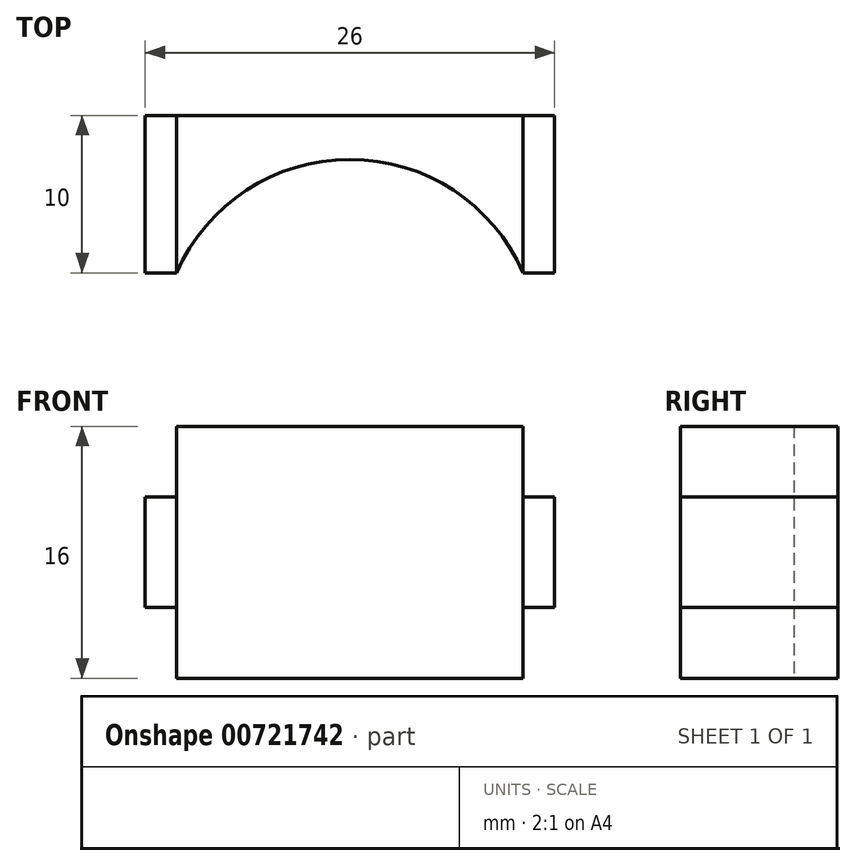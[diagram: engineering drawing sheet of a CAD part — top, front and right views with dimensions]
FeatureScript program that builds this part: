
annotation { "Feature Type Name" : "Feature", "Feature Type Description" : "" }
export const myFeature = defineFeature(function(context is Context, id is Id, definition is map)
    precondition{}
    {
        {
            var Q0;
            Q0=qCreatedBy(makeId("Top.planeOp"),FACE);
            var sketch = newSketch(context, id + "F0", { "sketchPlane" : qUnion([Q0])});
            skLineSegment(sketch, "E0", {"start": v(0, 0) * mm, "end": v(0, 10) * mm});
            skLineSegment(sketch, "E1", {"start": v(0, 10) * mm, "end": v(22, 10) * mm});
            skLineSegment(sketch, "E2", {"start": v(22, 10) * mm, "end": v(22, 0) * mm});
            skArc(sketch, "E3", {"start": v(22, 0) * mm, "mid": v(11, 7.2) * mm, "end": v(0, 0) * mm});
            skSolve(sketch);
        }
        {
            var Q0;
            Q0 = qSketchRegion(id + "F0", true);
            extrude(context, id + "F1", {"entities" : qUnion([Q0]), "depth" : 16 * mm, "offsetDistance" : 25 * mm});
        }
        {
            var Q0;
            Q0=makeQuery(id+"F1.opExtrude","SWEPT_FACE",FACE,{"disambiguationData":[OSD([sQuery(id+"F0.wireOp",EDGE,"E2")])]});
            var sketch = newSketch(context, id + "F2", { "sketchPlane" : qUnion([Q0])});
            skLineSegment(sketch, "E4.bottom", {"start": v(10, 11.5) * mm, "end": v(0, 11.5) * mm});
            skLineSegment(sketch, "E4.top", {"start": v(10, 4.5) * mm, "end": v(0, 4.5) * mm});
            skLineSegment(sketch, "E4.left", {"start": v(10, 11.5) * mm, "end": v(10, 4.5) * mm});
            skLineSegment(sketch, "E4.right", {"start": v(0, 11.5) * mm, "end": v(0, 4.5) * mm});
            skSolve(sketch);
        }
        {
            var Q0;
            Q0 = qSketchRegion(id + "F2", true);
            extrude(context, id + "F3", {"entities" : qUnion([Q0]), "operationType" : NewBodyOperationType.ADD, "depth" : 2 * mm, "offsetDistance" : 25 * mm});
        }
        {
            var Q0;
            Q0=makeQuery(id+"F1.opExtrude","SWEPT_FACE",FACE,{"disambiguationData":[OSD([sQuery(id+"F0.wireOp",EDGE,"E0")])]});
            var sketch = newSketch(context, id + "F4", { "sketchPlane" : qUnion([Q0])});
            skLineSegment(sketch, "E5.0.0", {"start": v(0, 4.5) * mm, "end": v(-10, 4.5) * mm});
            skLineSegment(sketch, "E5.0.1", {"start": v(-10, 4.5) * mm, "end": v(-10, 11.5) * mm});
            skLineSegment(sketch, "E5.0.2", {"start": v(-10, 11.5) * mm, "end": v(0, 11.5) * mm});
            skLineSegment(sketch, "E5.0.3", {"start": v(0, 11.5) * mm, "end": v(0, 4.5) * mm});
            skSolve(sketch);
        }
        {
            var Q0;
            Q0 = qSketchRegion(id + "F4", true);
            extrude(context, id + "F5", {"entities" : qUnion([Q0]), "operationType" : NewBodyOperationType.ADD, "depth" : 2 * mm, "offsetDistance" : 25 * mm});
        }
    });
